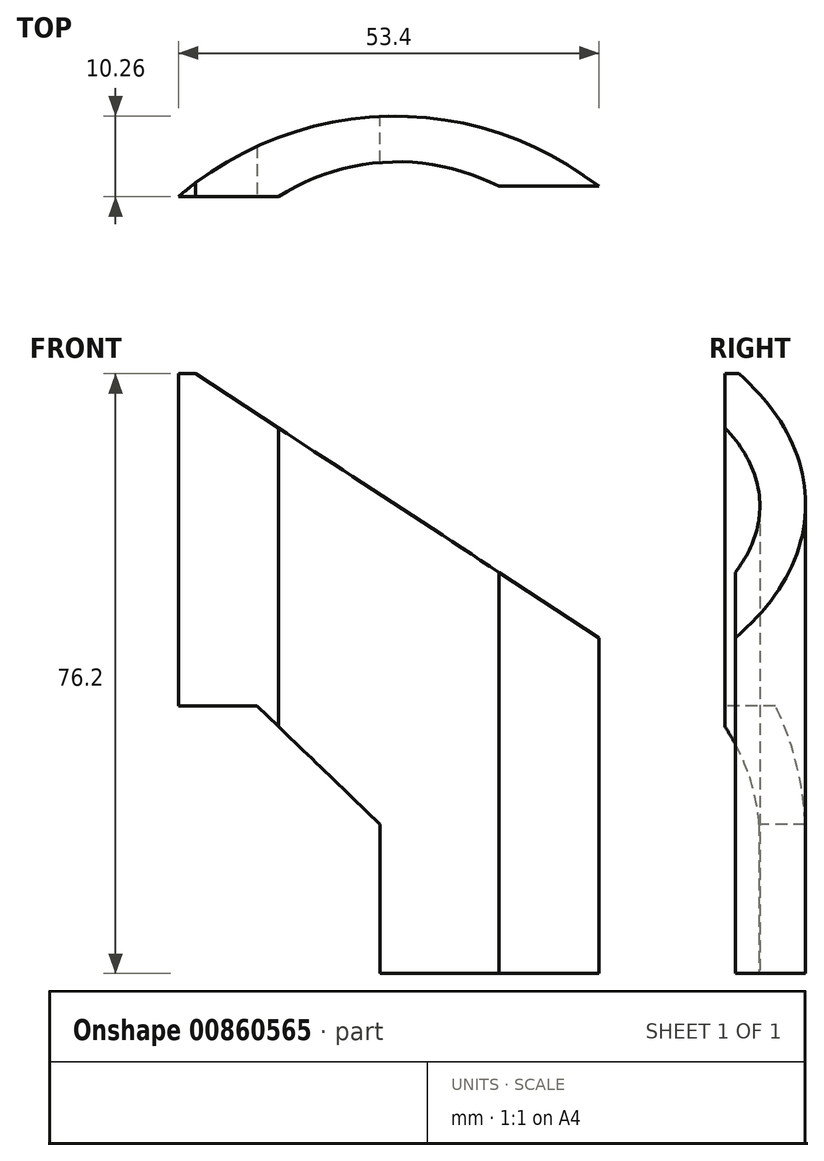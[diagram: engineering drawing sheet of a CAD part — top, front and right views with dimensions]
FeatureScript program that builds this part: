
annotation { "Feature Type Name" : "Feature", "Feature Type Description" : "" }
export const myFeature = defineFeature(function(context is Context, id is Id, definition is map)
    precondition{}
    {
        {
            var Q0;
            Q0=qCreatedBy(makeId("Top.planeOp"),FACE);
            var sketch = newSketch(context, id + "F0", { "sketchPlane" : qUnion([Q0])});
            skLineSegment(sketch, "E0", {"start": v(-16.44, 0) * mm, "end": v(-29.14, 0) * mm});
            skLineSegment(sketch, "E1.MirrorCS", {"start": v(0, 0) * mm, "end": v(0, -10.34) * mm});
            skLineSegment(sketch, "E2", {"start": v(11.56, 1.31) * mm, "end": v(24.26, 1.31) * mm});
            skArc(sketch, "E3", {"start": v(11.56, 1.31) * mm, "mid": v(-2.61, 4.41) * mm, "end": v(-16.44, 0) * mm});
            skArc(sketch, "E4", {"start": v(24.26, 1.31) * mm, "mid": v(-2.67, 10.25) * mm, "end": v(-29.14, 0) * mm});
            skSolve(sketch);
        }
        {
            var Q0;
            Q0=makeQuery(id+"F0.imprint","IMPRINT",FACE,{"disambiguationData":[TD([[makeQuery(id+"F0.imprint","IMPRINT",EDGE,{"derivedFrom":sQuery(id+"F0.wireOp",EDGE,"E0")}),-1.0]])]});
            extrude(context, id + "F1", {"entities" : qUnion([Q0]), "depth" : 76.2 * mm, "offsetDistance" : 25 * mm});
        }
        {
            var Q0;
            Q0=qCreatedBy(makeId("Front.planeOp"),FACE);
            var sketch = newSketch(context, id + "F2", { "sketchPlane" : qUnion([Q0])});
            skLineSegment(sketch, "E5", {"start": v(24.59, 78.81) * mm, "end": v(-30.96, 78.81) * mm});
            skLineSegment(sketch, "E6", {"start": v(-30.96, 78.81) * mm, "end": v(25.85, 41.63) * mm});
            skLineSegment(sketch, "E7", {"start": v(25.85, 41.63) * mm, "end": v(24.59, 78.81) * mm});
            skSolve(sketch);
        }
        {
            var Q0;
            Q0=makeQuery(id+"F2.imprint","IMPRINT",FACE,{"disambiguationData":[TD([[makeQuery(id+"F2.imprint","IMPRINT",EDGE,{"derivedFrom":sQuery(id+"F2.wireOp",EDGE,"E5")}),1.0]])]});
            extrude(context, id + "F3", {"entities" : qUnion([Q0]), "operationType" : NewBodyOperationType.REMOVE, "oppositeDirection" : true, "depth" : 25 * mm, "offsetDistance" : 25 * mm});
        }
        {
            var Q0;
            Q0=qCreatedBy(makeId("Front.planeOp"),FACE);
            var sketch = newSketch(context, id + "F4", { "sketchPlane" : qUnion([Q0])});
            skLineSegment(sketch, "E8.bottom", {"start": v(-3.55, -3.21) * mm, "end": v(-34.65, -3.21) * mm});
            skLineSegment(sketch, "E8.right", {"start": v(-34.65, -3.21) * mm, "end": v(-34.65, 34.03) * mm});
            skLineSegment(sketch, "E9", {"start": v(-3.55, 18.97) * mm, "end": v(-19.2, 34.03) * mm});
            skLineSegment(sketch, "E10", {"start": v(-3.55, -3.21) * mm, "end": v(-3.55, 18.97) * mm});
            skLineSegment(sketch, "E11", {"start": v(-19.2, 34.03) * mm, "end": v(-34.65, 34.03) * mm});
            skSolve(sketch);
        }
        {
            var Q0;
            Q0=makeQuery(id+"F4.imprint","IMPRINT",FACE,{"disambiguationData":[TD([[makeQuery(id+"F4.imprint","IMPRINT",EDGE,{"derivedFrom":sQuery(id+"F4.wireOp",EDGE,"E8.bottom")}),-1.0]])]});
            extrude(context, id + "F5", {"entities" : qUnion([Q0]), "operationType" : NewBodyOperationType.REMOVE, "oppositeDirection" : true, "depth" : 25 * mm, "offsetDistance" : 25 * mm});
        }
    });
